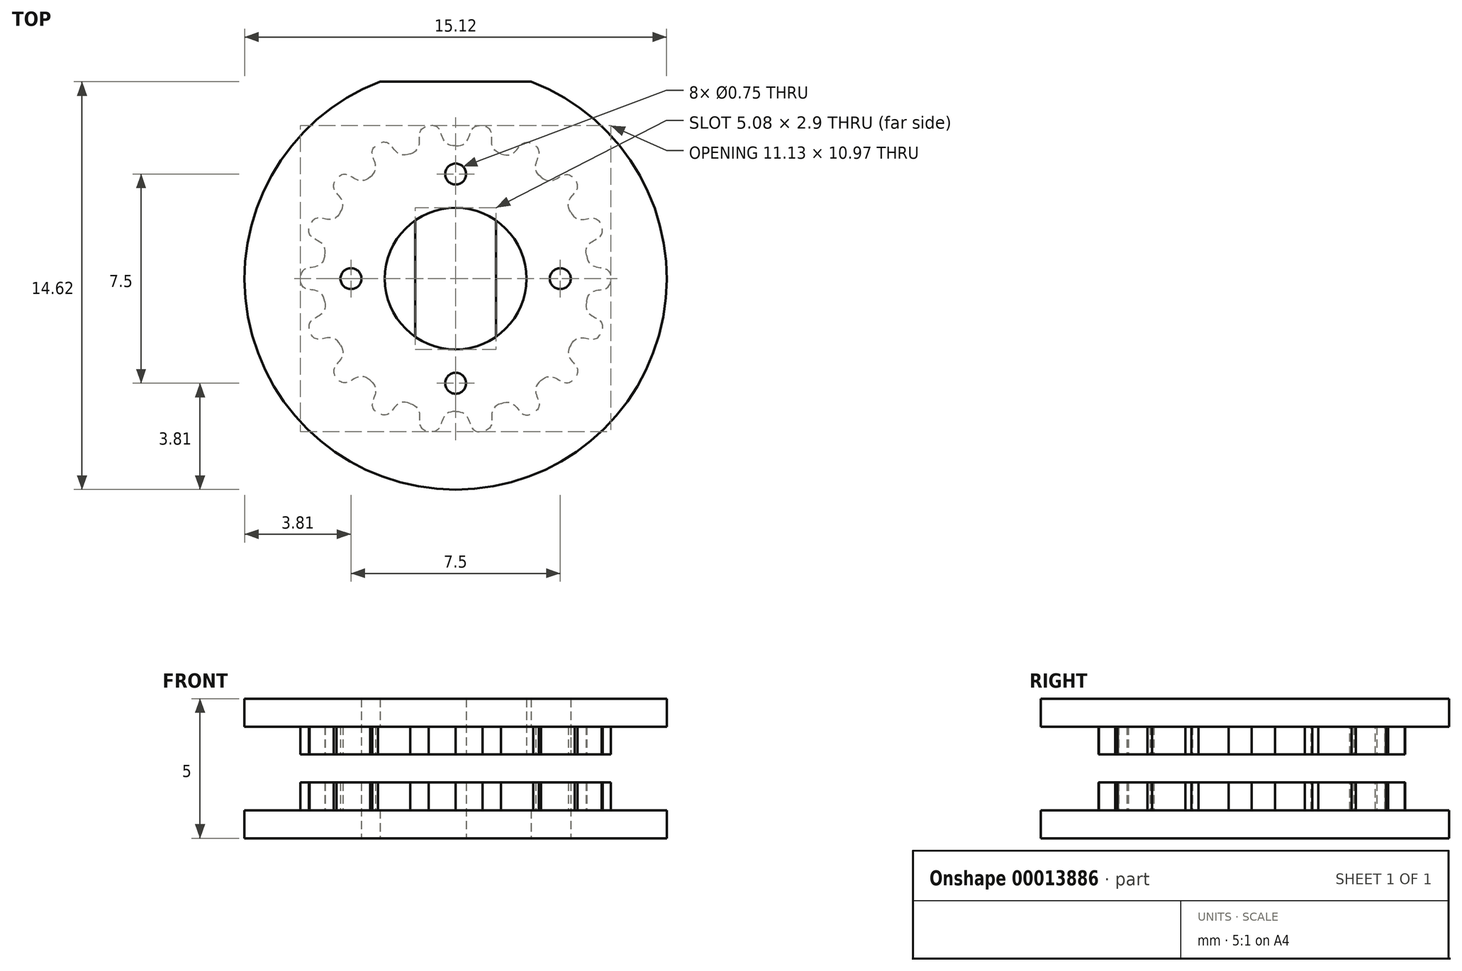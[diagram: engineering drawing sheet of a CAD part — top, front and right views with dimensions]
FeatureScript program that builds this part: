
annotation { "Feature Type Name" : "Feature", "Feature Type Description" : "" }
export const myFeature = defineFeature(function(context is Context, id is Id, definition is map)
    precondition{}
    {
        {
            assignVariable(context, id + "F0", {"name" : "teeth", "anyValue" : 18});
        }
        {
            var Q0;
            Q0=qCreatedBy(makeId("Top.planeOp"),FACE);
            var sketch = newSketch(context, id + "F1", { "sketchPlane" : qUnion([Q0])});
            skCircle(sketch, "E0", {"center": v(0, 0) * mm, "radius": 5.56 * mm, "construction": true});
            skLineSegment(sketch, "E1", {"start": v(0, 0) * mm, "end": v(0, 5.56) * mm, "construction": true});
            skLineSegment(sketch, "E2", {"start": v(0, 0) * mm, "end": v(0.97, 5.48) * mm, "construction": true});
            skArc(sketch, "E3", {"start": v(0.83, 4.7) * mm, "mid": v(0.42, 4.75) * mm, "end": v(0, 4.76) * mm, "construction": true});
            skLineSegment(sketch, "E4", {"start": v(0.61, 5.53) * mm, "end": v(0, 2.07) * mm, "construction": true});
            skFitSpline(sketch, "E5", {"points": [v(0, 4.76) * mm, v(0.58, 5.33) * mm, v(0.97, 5.48) * mm], "startDerivative": vector(2.43, -0.12) * mm, "endDerivative": vector(1.2, -0.2) * mm});
            skFitSpline(sketch, "E6.MirrorCS", {"points": [v(0, 4.76) * mm, v(-0.58, 5.33) * mm, v(-0.97, 5.48) * mm], "startDerivative": vector(-2.43, -0.12) * mm, "endDerivative": vector(-1.2, -0.2) * mm});
            skArc(sketch, "E7", {"start": v(0.97, 5.48) * mm, "mid": v(0, 5.56) * mm, "end": v(-0.97, 5.48) * mm});
            skLineSegment(sketch, "E8", {"start": v(-0.97, 5.48) * mm, "end": v(-1.66, 9.42) * mm});
            skArc(sketch, "E9", {"start": v(1.66, 9.42) * mm, "mid": v(0, 9.56) * mm, "end": v(-1.66, 9.42) * mm});
            skLineSegment(sketch, "E10", {"start": v(1.66, 9.42) * mm, "end": v(0.97, 5.48) * mm});
            skSolve(sketch);
        }
        {
            var Q0;
            Q0=qCreatedBy(makeId("Top.planeOp"),FACE);
            var sketch = newSketch(context, id + "F2", { "sketchPlane" : qUnion([Q0])});
            skCircle(sketch, "E11", {"center": v(0, 0) * mm, "radius": 7.56 * mm});
            skCircle(sketch, "E12", {"center": v(0, 0) * mm, "radius": 2.54 * mm});
            skLineSegment(sketch, "E13", {"start": v(-1.45, 2.09) * mm, "end": v(-1.45, -2.09) * mm});
            skLineSegment(sketch, "E14", {"start": v(1.45, 2.09) * mm, "end": v(1.45, -2.09) * mm});
            skCircle(sketch, "E15", {"center": v(-3.75, 0) * mm, "radius": 0.38 * mm});
            skCircle(sketch, "E16", {"center": v(3.75, 0) * mm, "radius": 0.38 * mm});
            skLineSegment(sketch, "E17", {"start": v(-3.75, 0) * mm, "end": v(3.75, 0) * mm, "construction": true});
            skLineSegment(sketch, "E18", {"start": v(-2.7, 7.06) * mm, "end": v(2.7, 7.06) * mm});
            skCircle(sketch, "E19", {"center": v(0, -3.75) * mm, "radius": 0.38 * mm});
            skCircle(sketch, "E20", {"center": v(0, 3.75) * mm, "radius": 0.38 * mm});
            skSolve(sketch);
        }
        {
            var Q0;
            Q0=makeQuery(id+"F2.imprint","IMPRINT",FACE,{"disambiguationData":[TD([[makeQuery(id+"F2.imprint","IMPRINT",EDGE,{"derivedFrom":sQuery(id+"F2.wireOp",EDGE,"E15")}),-1.0]])]});
            var Q1;
            {var subQ7=sQuery(id+"F2.wireOp",EDGE,"E18");Q1=makeQuery(id+"F2.imprint","IMPRINT",FACE,{"disambiguationData":[TD([[makeQuery(id+"F2.imprint","IMPRINT",EDGE,{"derivedFrom":subQ7}),-1.0]])]});}
            extrude(context, id + "F3", {"entities" : qUnion([Q0, Q1]), "depth" : 2.5 * mm, "offsetDistance" : 25 * mm});
        }
        {
            var Q0;
            {var subQ7=sQuery(id+"F2.wireOp",EDGE,"E18");Q0=makeQuery(id+"F2.imprint","IMPRINT",FACE,{"disambiguationData":[TD([[makeQuery(id+"F2.imprint","IMPRINT",EDGE,{"derivedFrom":subQ7}),-1.0]])]});}
            var Q1;
            {var subQ0=sQuery(id+"F2.wireOp",EDGE,"E13");Q1=makeQuery(id+"F2.imprint","IMPRINT",FACE,{"disambiguationData":[TD([[makeQuery(id+"F2.imprint","IMPRINT",EDGE,{"derivedFrom":subQ0}),-1.0]])]});}
            var Q2;
            {var subQ0=sQuery(id+"F2.wireOp",EDGE,"E14");Q2=makeQuery(id+"F2.imprint","IMPRINT",FACE,{"disambiguationData":[TD([[makeQuery(id+"F2.imprint","IMPRINT",EDGE,{"derivedFrom":subQ0}),1.0]])]});}
            extrude(context, id + "F4", {"entities" : qUnion([Q0, Q1, Q2]), "operationType" : NewBodyOperationType.ADD, "oppositeDirection" : true, "depth" : 2.5 * mm, "offsetDistance" : 25 * mm});
        }
        {
            var Q0;
            Q0=qSketchRegion(id+"F1",true);
            extrude(context, id + "F5", {"entities" : qUnion([Q0]), "endBound" : BoundingType.SYMMETRIC, "depth" : 3 * mm, "offsetDistance" : 25 * mm});
        }
        {
            var Q0;
            Q0=makeQuery(id+"F5.opExtrude","SWEPT_BODY",BODY,{"disambiguationData":[OSD([sQuery(id+"F1.wireOp",EDGE,"E5"),sQuery(id+"F1.wireOp",EDGE,"E6.MirrorCS"),sQuery(id+"F1.wireOp",EDGE,"E7")])]});
            var Q1;
            Q1=sQuery(id+"F1.wireOp",EDGE,"E0");
            circularPattern(context, id + "F6", {"operationType" : NewBodyOperationType.REMOVE, "entities" : qUnion([Q0]), "axis" : qUnion([Q1]), "angle" : 360 * degree, "instanceCount" : getVariable(context, 'teeth'), "equalSpace" : true});
        }
        {
            var Q0;
            Q0=qSketchRegion(id+"F2",true);
            var Q1;
            {var subQ0=sQuery(id+"F2.wireOp",EDGE,"E14");Q1=makeQuery(id+"F2.imprint","IMPRINT",FACE,{"disambiguationData":[TD([[makeQuery(id+"F2.imprint","IMPRINT",EDGE,{"derivedFrom":subQ0}),1.0]])]});}
            var Q2;
            {var subQ0=sQuery(id+"F2.wireOp",EDGE,"E13");Q2=makeQuery(id+"F2.imprint","IMPRINT",FACE,{"disambiguationData":[TD([[makeQuery(id+"F2.imprint","IMPRINT",EDGE,{"derivedFrom":subQ0}),1.0]])]});}
            var Q3;
            {var subQ0=sQuery(id+"F2.wireOp",EDGE,"E13");Q3=makeQuery(id+"F2.imprint","IMPRINT",FACE,{"disambiguationData":[TD([[makeQuery(id+"F2.imprint","IMPRINT",EDGE,{"derivedFrom":subQ0}),-1.0]])]});}
            extrude(context, id + "F7", {"entities" : qUnion([Q0, Q1, Q2, Q3]), "operationType" : NewBodyOperationType.REMOVE, "endBound" : BoundingType.SYMMETRIC, "oppositeDirection" : true, "depth" : 1 * mm, "offsetDistance" : 25 * mm});
        }
        {
            var Q0;
            Q0=makeQuery(id+"F7.boolean.opBoolean","SPLIT",BODY,{"disambiguationData":[OD(0.0)],"derivedFrom":makeQuery(id+"F3.opExtrude","SWEPT_BODY",BODY,{"disambiguationData":[OSD([sQuery(id+"F2.wireOp",EDGE,"E11"),sQuery(id+"F2.wireOp",EDGE,"E12"),sQuery(id+"F2.wireOp",EDGE,"E13"),sQuery(id+"F2.wireOp",EDGE,"E14")])]})});
            transform(context, id + "F8", {"entities" : qUnion([Q0]), "transformType" : TransformType.TRANSLATION_3D, "dx" : 0 * mm, "dy" : 0 * mm, "dz" : -10 * mm, "makeCopy" : false});
        }
    });
